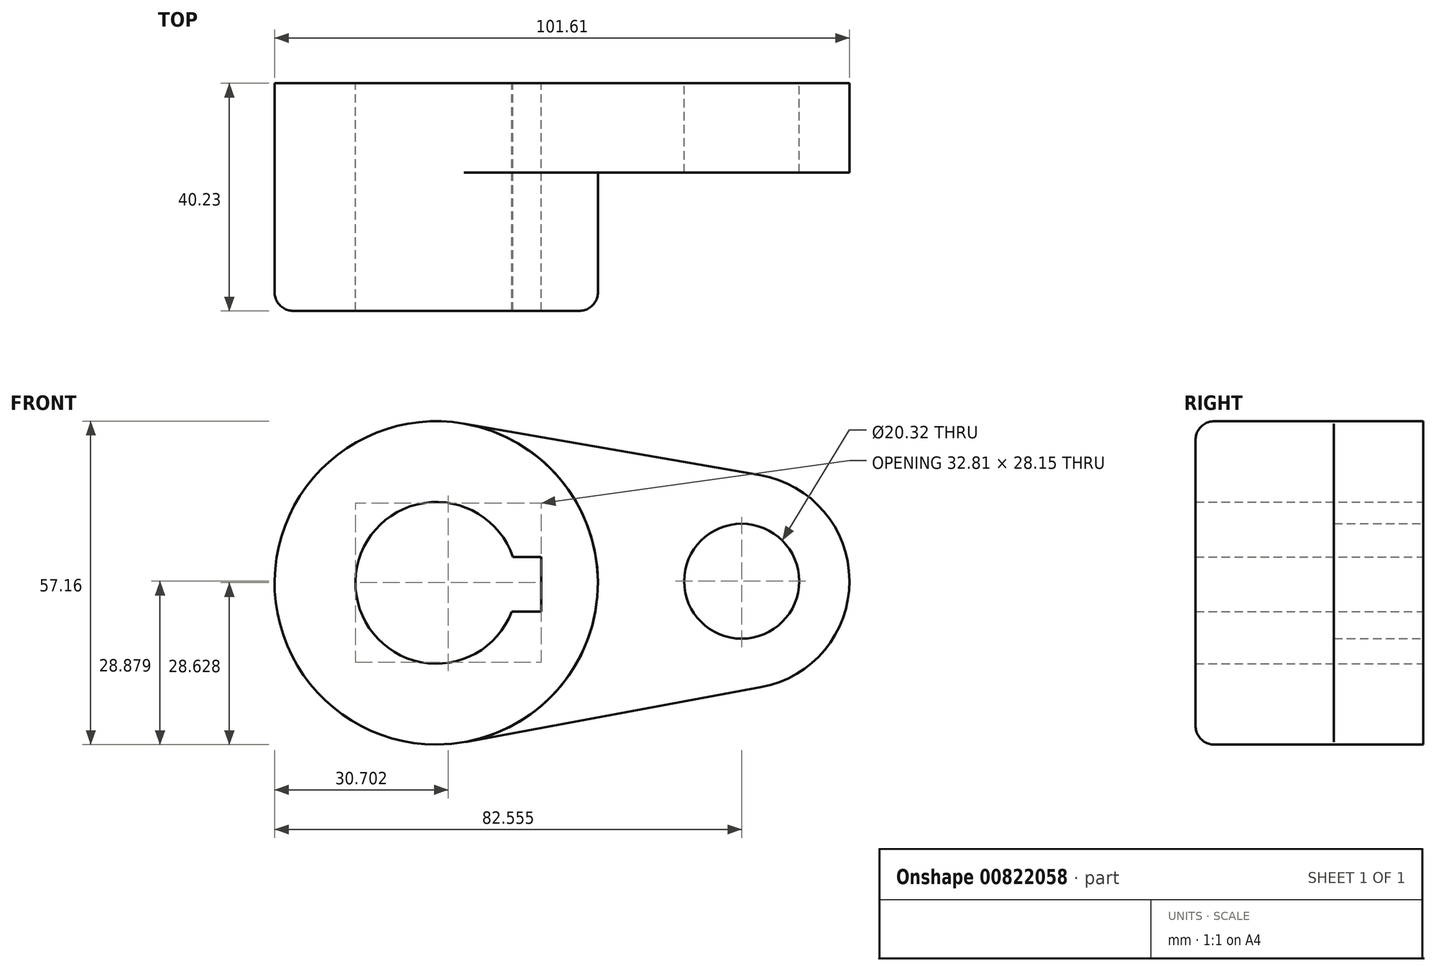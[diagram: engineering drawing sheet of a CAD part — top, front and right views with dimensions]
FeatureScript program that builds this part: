
annotation { "Feature Type Name" : "Feature", "Feature Type Description" : "" }
export const myFeature = defineFeature(function(context is Context, id is Id, definition is map)
    precondition{}
    {
        {
            var Q0;
            Q0=qCreatedBy(makeId("Front.planeOp"),FACE);
            var sketch = newSketch(context, id + "F0", { "sketchPlane" : qUnion([Q0])});
            skCircle(sketch, "E0", {"center": v(0, 0) * mm, "radius": 28.58 * mm});
            skArc(sketch, "E1", {"start": v(13.54, 4.56) * mm, "mid": v(-14.28, 0.28) * mm, "end": v(13.35, -5.09) * mm});
            skLineSegment(sketch, "E2", {"start": v(4.89, 28.15) * mm, "end": v(57.23, 19.07) * mm});
            skLineSegment(sketch, "E3", {"start": v(5.2, -28.1) * mm, "end": v(57.44, -18.43) * mm});
            skArc(sketch, "E4", {"start": v(57.44, -18.43) * mm, "mid": v(73.02, 0.4) * mm, "end": v(57.23, 19.07) * mm});
            skCircle(sketch, "E5", {"center": v(53.98, 0.3) * mm, "radius": 10.16 * mm});
            skLineSegment(sketch, "E6", {"start": v(13.54, 4.56) * mm, "end": v(18.53, 4.56) * mm});
            skLineSegment(sketch, "E7", {"start": v(18.53, -5.09) * mm, "end": v(13.35, -5.09) * mm});
            skLineSegment(sketch, "E8", {"start": v(18.53, 4.56) * mm, "end": v(18.53, -5.09) * mm});
            skSolve(sketch);
        }
        {
            var Q0;
            {var subQ0=sQuery(id+"F0.wireOp",EDGE,"E6");Q0=makeQuery(id+"F0.imprint","IMPRINT",FACE,{"disambiguationData":[TD([[makeQuery(id+"F0.imprint","IMPRINT",EDGE,{"derivedFrom":subQ0}),1.0]])]});}
            extrude(context, id + "F1", {"entities" : qUnion([Q0]), "depth" : 40.23 * mm, "offsetDistance" : 25.4 * mm});
        }
        {
            var Q0;
            {var subQ0=sQuery(id+"F0.wireOp",EDGE,"E2");Q0=makeQuery(id+"F0.imprint","IMPRINT",FACE,{"disambiguationData":[TD([[makeQuery(id+"F0.imprint","IMPRINT",EDGE,{"derivedFrom":subQ0}),-1.0]])]});}
            extrude(context, id + "F2", {"entities" : qUnion([Q0]), "operationType" : NewBodyOperationType.ADD, "depth" : 15.77 * mm, "offsetDistance" : 25.4 * mm});
        }
        {
            var Q0;
            Q0=makeQuery(id+"F1.opExtrude","CAP_EDGE",EDGE,{"disambiguationData":[OSD([sQuery(id+"F0.wireOp",EDGE,"E0")])],"isStart":false});
            fillet(context, id + "F3", {"entities" : qUnion([Q0]), "radius" : 3.3 * mm, "tangentPropagation" : true, "allowEdgeOverflow" : false});
        }
    });
